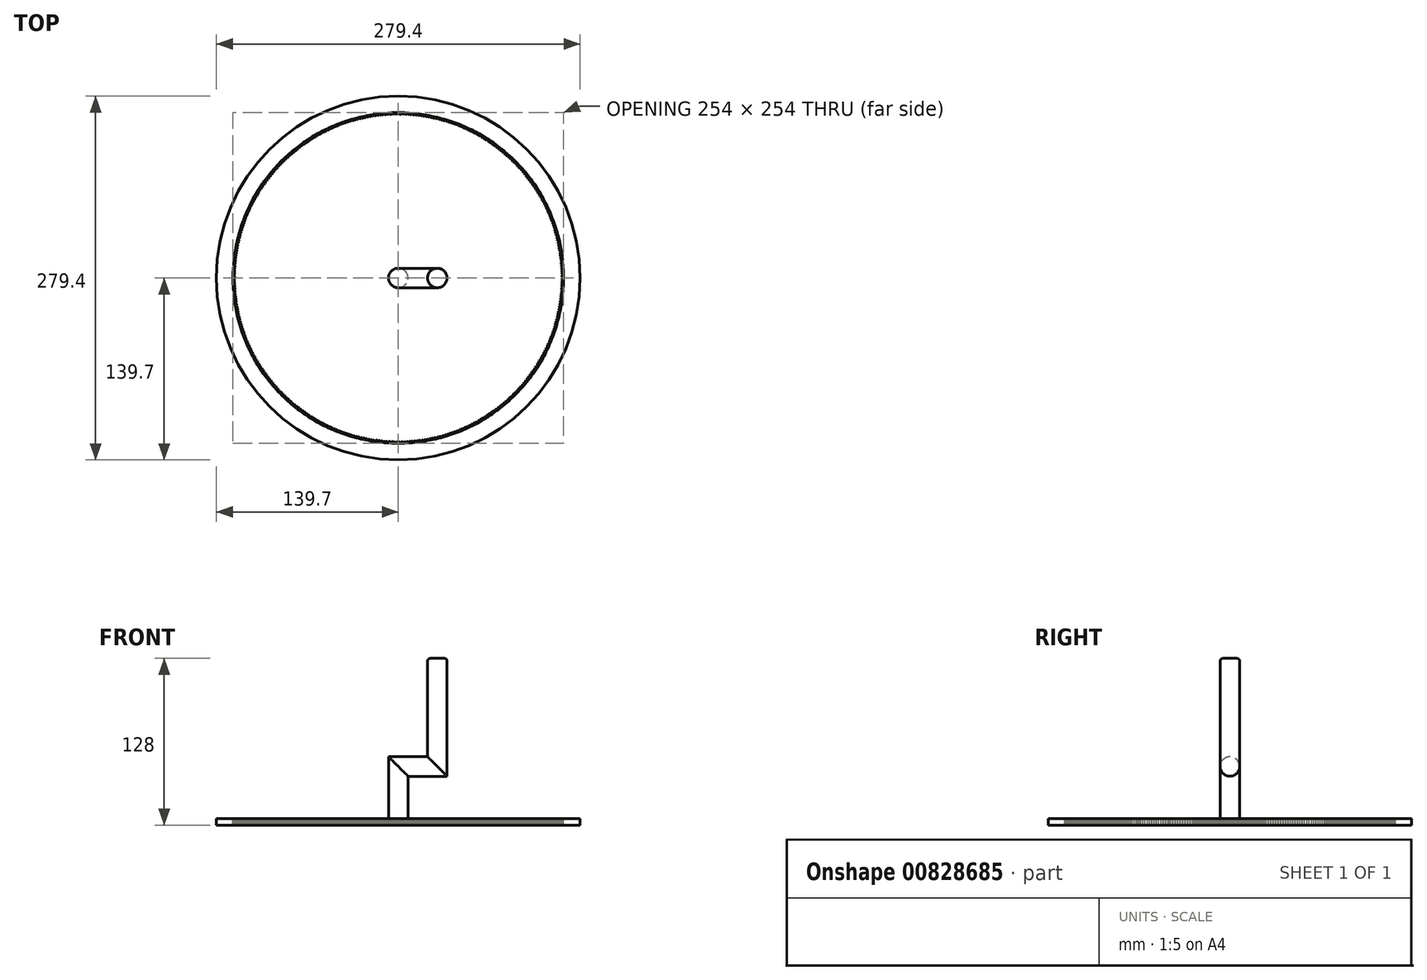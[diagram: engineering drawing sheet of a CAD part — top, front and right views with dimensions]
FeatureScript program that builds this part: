
annotation { "Feature Type Name" : "Feature", "Feature Type Description" : "" }
export const myFeature = defineFeature(function(context is Context, id is Id, definition is map)
    precondition{}
    {
        {
            var Q0;
            Q0=qCreatedBy(makeId("Front.planeOp"),FACE);
            var sketch = newSketch(context, id + "F0", { "sketchPlane" : qUnion([Q0])});
            skLineSegment(sketch, "E0", {"start": v(0, 0) * mm, "end": v(0, 40) * mm});
            skLineSegment(sketch, "E1", {"start": v(0, 40) * mm, "end": v(30, 40) * mm});
            skLineSegment(sketch, "E2", {"start": v(30, 40) * mm, "end": v(30, 123) * mm});
            skSolve(sketch);
        }
        {
            var Q0;
            Q0=qCreatedBy(makeId("Top.planeOp"),FACE);
            var sketch = newSketch(context, id + "F1", { "sketchPlane" : qUnion([Q0])});
            skCircle(sketch, "E3", {"center": v(0, 0) * mm, "radius": 7.5 * mm});
            skSolve(sketch);
        }
        {
            var Q0;
            Q0=makeQuery(id+"F1.imprint","IMPRINT",FACE,{"disambiguationData":[TD([[makeQuery(id+"F1.imprint","IMPRINT",EDGE,{"derivedFrom":sQuery(id+"F1.wireOp",EDGE,"E3")}),1.0]])]});
            var Q1;
            Q1=sQuery(id+"F0.wireOp",EDGE,"E0");
            var Q2;
            Q2=sQuery(id+"F0.wireOp",EDGE,"E1");
            var Q3;
            Q3=sQuery(id+"F0.wireOp",EDGE,"E2");
            sweep(context, id + "F2", {"profiles" : qUnion([Q0]), "path" : qUnion([Q1, Q2, Q3])});
        }
        {
            var Q0;
            Q0=makeQuery(id+"F2.opSweep","CAP_EDGE",EDGE,{"disambiguationData":[OSD([sQuery(id+"F0.wireOp",VERTEX,"E2.end"),sQuery(id+"F1.wireOp",EDGE,"E3")])],"isStart":false});
            fillet(context, id + "F3", {"entities" : qUnion([Q0]), "radius" : 2 * mm, "tangentPropagation" : true, "allowEdgeOverflow" : false});
        }
        {
            var Q0;
            Q0=qCreatedBy(makeId("Top.planeOp"),FACE);
            var sketch = newSketch(context, id + "F4", { "sketchPlane" : qUnion([Q0])});
            skCircle(sketch, "E4", {"center": v(0, 0) * mm, "radius": 139.7 * mm});
            skCircle(sketch, "E5", {"center": v(0, 0) * mm, "radius": 127 * mm});
            skLineSegment(sketch, "E6.2.1", {"start": v(5, 0) * mm, "end": v(-5, 0) * mm});
            skPoint(sketch, "E7", {"position": v(0, -127) * mm});
            skLineSegment(sketch, "E8", {"start": v(-5, 0) * mm, "end": v(-5, -127) * mm});
            skLineSegment(sketch, "E9.MirrorCS", {"start": v(5, 0) * mm, "end": v(5, -127) * mm});
            skLineSegment(sketch, "E10", {"start": v(-5, -127) * mm, "end": v(5, -127) * mm});
            skLineSegment(sketch, "E11", {"start": v(-1, -126.96) * mm, "end": v(1, -126.96) * mm});
            skLineSegment(sketch, "E12", {"start": v(-1, -126.96) * mm, "end": v(0, -125.22) * mm});
            skLineSegment(sketch, "E13", {"start": v(0, -125.22) * mm, "end": v(1, -126.96) * mm});
            skLineSegment(sketch, "E14.1.0", {"start": v(0, -5) * mm, "end": v(127, -5) * mm});
            skLineSegment(sketch, "E14.1.1", {"start": v(0, 5) * mm, "end": v(127, 5) * mm});
            skLineSegment(sketch, "E14.1.2", {"start": v(127, -5) * mm, "end": v(127, 5) * mm});
            skLineSegment(sketch, "E14.1.3", {"start": v(0, 5) * mm, "end": v(0, -5) * mm});
            skLineSegment(sketch, "E14.2.0", {"start": v(5, 0) * mm, "end": v(5, 127) * mm});
            skLineSegment(sketch, "E14.2.1", {"start": v(-5, 0) * mm, "end": v(-5, 127) * mm});
            skLineSegment(sketch, "E14.2.2", {"start": v(5, 127) * mm, "end": v(-5, 127) * mm});
            skLineSegment(sketch, "E14.2.3", {"start": v(-5, 0) * mm, "end": v(5, 0) * mm});
            skLineSegment(sketch, "E14.3.0", {"start": v(0, 5) * mm, "end": v(-127, 5) * mm});
            skLineSegment(sketch, "E14.3.1", {"start": v(0, -5) * mm, "end": v(-127, -5) * mm});
            skLineSegment(sketch, "E14.3.2", {"start": v(-127, 5) * mm, "end": v(-127, -5) * mm});
            skLineSegment(sketch, "E14.3.3", {"start": v(0, -5) * mm, "end": v(0, 5) * mm});
            skSolve(sketch);
        }
        {
            var Q0;
            Q0=qCreatedBy(makeId("Right.planeOp"),FACE);
            var sketch = newSketch(context, id + "F5", { "sketchPlane" : qUnion([Q0])});
            skLineSegment(sketch, "E15", {"start": v(0, -53.17) * mm, "end": v(0, 127.13) * mm});
            skSolve(sketch);
        }
        {
            var Q0;
            Q0=makeQuery(id+"F4.imprint","IMPRINT",FACE,{"disambiguationData":[TD([[makeQuery(id+"F4.imprint","IMPRINT",EDGE,{"derivedFrom":sQuery(id+"F4.wireOp",EDGE,"cf0199a6-fa25-477d-ac96-ee3429343f3a.2.0")}),-1.0]])]});
            var Q1;
            Q1=makeQuery(id+"F4.imprint","IMPRINT",FACE,{"disambiguationData":[TD([[makeQuery(id+"F4.imprint","IMPRINT",EDGE,{"derivedFrom":sQuery(id+"F4.wireOp",EDGE,"E4")}),1.0]])]});
            var Q2;
            Q2=makeQuery(id+"F4.imprint","IMPRINT",FACE,{"disambiguationData":[TD([[makeQuery(id+"F4.imprint","IMPRINT",EDGE,{"derivedFrom":sQuery(id+"F4.wireOp",EDGE,"E11")}),1.0]])]});
            var Q3;
            {var subQ0=sQuery(id+"F4.wireOp",EDGE,"E10");var subQ1=sQuery(id+"F4.wireOp",EDGE,"E5");var subQ2=makeQuery(id+"F4.imprint","INTERSECT",VERTEX,{"derivedFrom":[subQ1,subQ0]});Q3=makeQuery(id+"F4.imprint","IMPRINT",FACE,{"disambiguationData":[TD([[makeQuery(id+"F4.imprint","IMPRINT",EDGE,{"disambiguationData":[TD([[subQ2,-1.0]])],"derivedFrom":subQ1}),-1.0]])]});}
            var Q4;
            {var subQ0=sQuery(id+"F4.wireOp",EDGE,"E8");var subQ1=sQuery(id+"F4.wireOp",EDGE,"E5");var subQ2=makeQuery(id+"F4.imprint","INTERSECT",VERTEX,{"derivedFrom":[subQ1,subQ0]});Q4=makeQuery(id+"F4.imprint","IMPRINT",FACE,{"disambiguationData":[TD([[makeQuery(id+"F4.imprint","IMPRINT",EDGE,{"disambiguationData":[TD([[subQ2,-1.0]])],"derivedFrom":subQ1}),-1.0]])]});}
            extrude(context, id + "F6", {"entities" : qUnion([Q0, Q1, Q2, Q3, Q4]), "oppositeDirection" : true, "depth" : 5 * mm, "offsetDistance" : 25.4 * mm});
        }
        {
            var Q0;
            Q0=makeQuery(id+"F6.opExtrude","SWEPT_BODY",BODY,{"disambiguationData":[OSD([sQuery(id+"F4.wireOp",EDGE,"E11"),sQuery(id+"F4.wireOp",EDGE,"E12"),sQuery(id+"F4.wireOp",EDGE,"E13")])]});
            var Q1;
            Q1=makeQuery(id+"F6.opExtrude","SWEPT_FACE",FACE,{"disambiguationData":[OSD([sQuery(id+"F4.wireOp",EDGE,"cf0199a6-fa25-477d-ac96-ee3429343f3a.2.2")])]});
            var Q2;
            Q2=sQuery(id+"F5.wireOp",EDGE,"E15");
            circularPattern(context, id + "F7", {"entities" : qUnion([Q0]), "axis" : qUnion([Q2]), "angle" : 360 * degree, "instanceCount" : 399, "equalSpace" : true});
        }
    });
